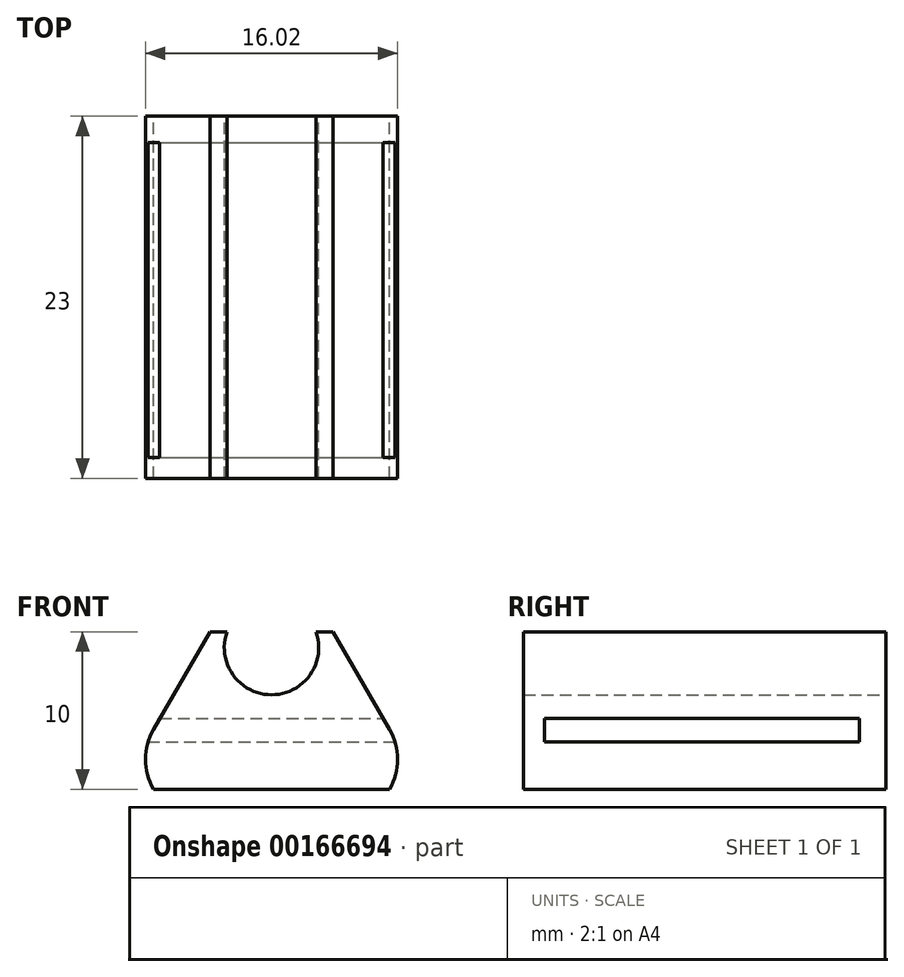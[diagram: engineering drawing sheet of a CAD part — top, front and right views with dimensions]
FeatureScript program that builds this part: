
annotation { "Feature Type Name" : "Feature", "Feature Type Description" : "" }
export const myFeature = defineFeature(function(context is Context, id is Id, definition is map)
    precondition{}
    {
        {
            assignVariable(context, id + "F0", {"name" : "length", "anyValue" : 23});
        }
        {
            var Q0;
            Q0=qCreatedBy(makeId("Front.planeOp"),FACE);
            var sketch = newSketch(context, id + "F1", { "sketchPlane" : qUnion([Q0])});
            skArc(sketch, "E0", {"start": v(-2.83, 10) * mm, "mid": v(0, 6) * mm, "end": v(2.83, 10) * mm});
            skLineSegment(sketch, "E1", {"start": v(2.83, 10) * mm, "end": v(3.91, 10) * mm});
            skLineSegment(sketch, "E2", {"start": v(3.91, 10) * mm, "end": v(7.5, 3.8) * mm});
            skArc(sketch, "E3", {"start": v(7.5, 0) * mm, "mid": v(8.01, 1.9) * mm, "end": v(7.5, 3.8) * mm});
            skLineSegment(sketch, "E4", {"start": v(7.5, 0) * mm, "end": v(-7.5, 0) * mm});
            skLineSegment(sketch, "E5", {"start": v(-2.83, 10) * mm, "end": v(-3.91, 10) * mm});
            skLineSegment(sketch, "E6", {"start": v(-3.91, 10) * mm, "end": v(-7.5, 3.8) * mm});
            skArc(sketch, "E7", {"start": v(-7.5, 3.8) * mm, "mid": v(-8.01, 1.9) * mm, "end": v(-7.5, 0) * mm});
            skSolve(sketch);
        }
        {
            var Q0;
            Q0=makeQuery(id+"F1.imprint","IMPRINT",FACE,{"disambiguationData":[TD([[makeQuery(id+"F1.imprint","IMPRINT",EDGE,{"derivedFrom":sQuery(id+"F1.wireOp",EDGE,"E0")}),-1.0]])]});
            extrude(context, id + "F2", {"entities" : qUnion([Q0]), "depth" : (getVariable(context, 'length')) * mm, "symmetric" : true});
        }
        {
            var Q0;
            Q0=qCreatedBy(makeId("Right.planeOp"),FACE);
            var sketch = newSketch(context, id + "F3", { "sketchPlane" : qUnion([Q0])});
            skLineSegment(sketch, "E8.bottom", {"start": v(9.84, 4.5) * mm, "end": v(-10.16, 4.5) * mm});
            skLineSegment(sketch, "E8.top", {"start": v(9.84, 3) * mm, "end": v(-10.16, 3) * mm});
            skLineSegment(sketch, "E8.left", {"start": v(9.84, 4.5) * mm, "end": v(9.84, 3) * mm});
            skLineSegment(sketch, "E8.right", {"start": v(-10.16, 4.5) * mm, "end": v(-10.16, 3) * mm});
            skSolve(sketch);
        }
        {
            var Q0;
            Q0=qSketchRegion(id+"F3",true);
            extrude(context, id + "F4", {"entities" : qUnion([Q0]), "operationType" : NewBodyOperationType.REMOVE, "oppositeDirection" : true, "depth" : 25 * mm, "symmetric" : true});
        }
    });
